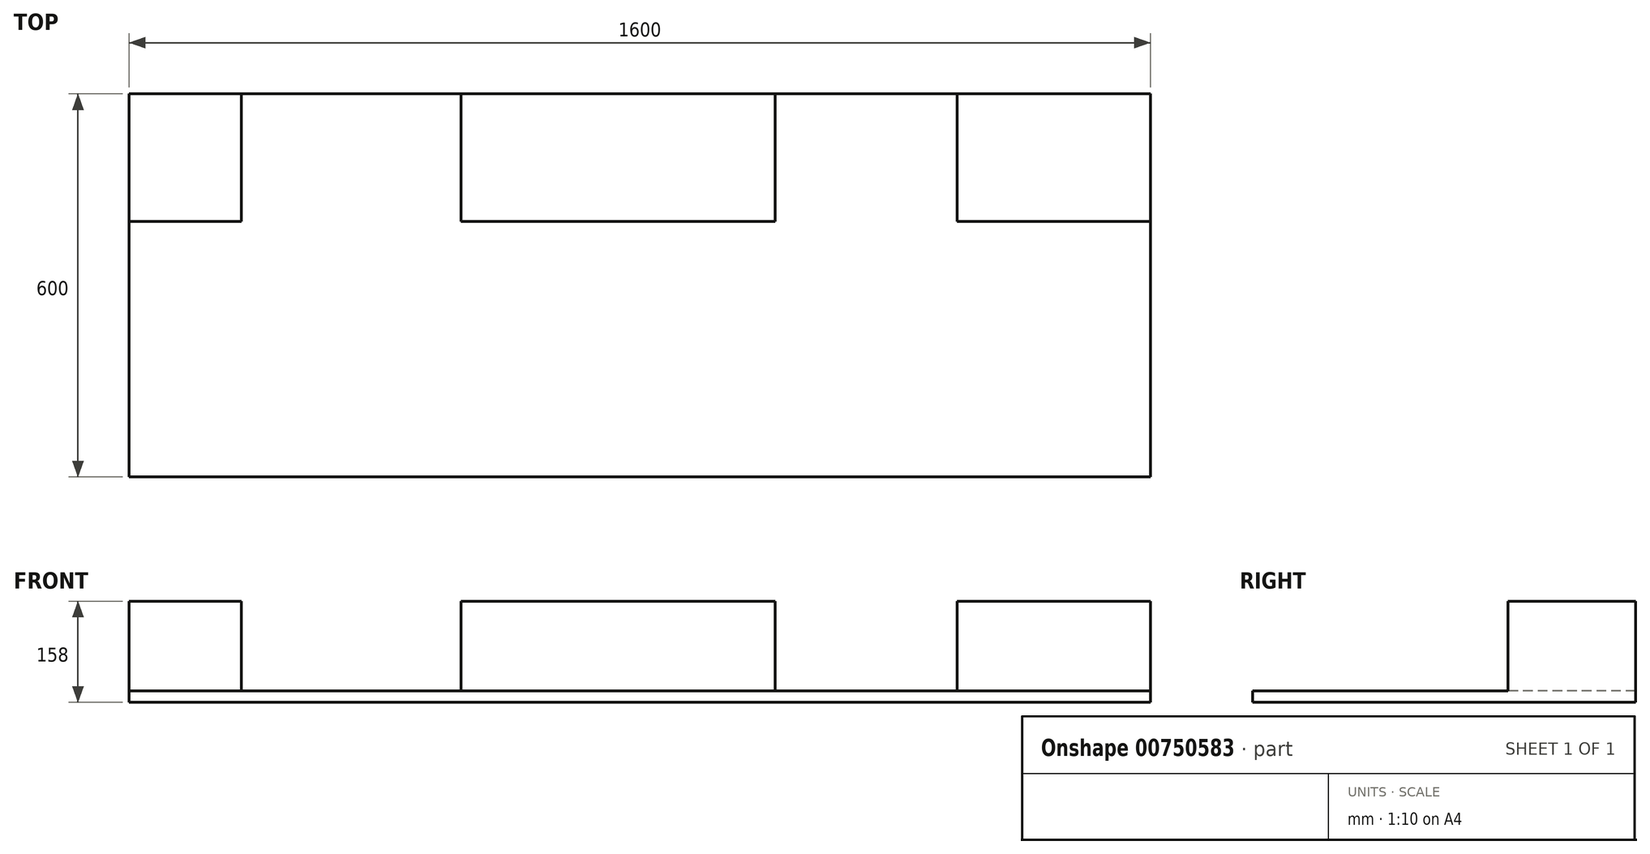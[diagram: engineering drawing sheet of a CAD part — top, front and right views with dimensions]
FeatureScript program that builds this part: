
annotation { "Feature Type Name" : "Feature", "Feature Type Description" : "" }
export const myFeature = defineFeature(function(context is Context, id is Id, definition is map)
    precondition{}
    {
        {
            var Q0;
            Q0=qCreatedBy(makeId("Top.planeOp"),FACE);
            var sketch = newSketch(context, id + "F0", { "sketchPlane" : qUnion([Q0])});
            skLineSegment(sketch, "E0.bottom", {"start": v(800, -300) * mm, "end": v(-800, -300) * mm});
            skLineSegment(sketch, "E0.top", {"start": v(800, 300) * mm, "end": v(-800, 300) * mm});
            skLineSegment(sketch, "E0.left", {"start": v(800, -300) * mm, "end": v(800, 300) * mm});
            skLineSegment(sketch, "E0.right", {"start": v(-800, -300) * mm, "end": v(-800, 300) * mm});
            skPoint(sketch, "E0.middle", {"position": v(0, 0) * mm});
            skSolve(sketch);
        }
        {
            var Q0;
            Q0=qSketchRegion(id+"F0",true);
            extrude(context, id + "F1", {"entities" : qUnion([Q0]), "depth" : 18 * mm, "offsetDistance" : 25 * mm});
        }
        {
            var Q0;
            Q0=makeQuery(id+"F1.opExtrude","CAP_FACE",FACE,{"disambiguationData":[OSD([sQuery(id+"F0.wireOp",EDGE,"E0.bottom"),sQuery(id+"F0.wireOp",EDGE,"E0.top"),sQuery(id+"F0.wireOp",EDGE,"E0.left"),sQuery(id+"F0.wireOp",EDGE,"E0.right")])],"isStart":false});
            var sketch = newSketch(context, id + "F2", { "sketchPlane" : qUnion([Q0])});
            skLineSegment(sketch, "E1.bottom", {"start": v(-800, 300) * mm, "end": v(-624.22, 300) * mm});
            skLineSegment(sketch, "E1.top", {"start": v(-800, 100) * mm, "end": v(-624.22, 100) * mm});
            skLineSegment(sketch, "E1.left", {"start": v(-800, 300) * mm, "end": v(-800, 100) * mm});
            skLineSegment(sketch, "E1.right", {"start": v(-624.22, 300) * mm, "end": v(-624.22, 100) * mm});
            skLineSegment(sketch, "E2.bottom", {"start": v(800, 300) * mm, "end": v(497, 300) * mm});
            skLineSegment(sketch, "E2.top", {"start": v(800, 100) * mm, "end": v(497, 100) * mm});
            skLineSegment(sketch, "E2.left", {"start": v(800, 300) * mm, "end": v(800, 100) * mm});
            skLineSegment(sketch, "E2.right", {"start": v(497, 300) * mm, "end": v(497, 100) * mm});
            skLineSegment(sketch, "E3.bottom", {"start": v(-280.3, 300) * mm, "end": v(212.39, 300) * mm});
            skLineSegment(sketch, "E3.top", {"start": v(-280.3, 100) * mm, "end": v(212.39, 100) * mm});
            skLineSegment(sketch, "E3.left", {"start": v(-280.3, 300) * mm, "end": v(-280.3, 100) * mm});
            skLineSegment(sketch, "E3.right", {"start": v(212.39, 300) * mm, "end": v(212.39, 100) * mm});
            skSolve(sketch);
        }
        {
            var Q0;
            Q0=makeQuery(id+"F2.imprint","IMPRINT",FACE,{"disambiguationData":[TD([[makeQuery(id+"F2.imprint","IMPRINT",EDGE,{"derivedFrom":sQuery(id+"F2.wireOp",EDGE,"E2.bottom")}),1.0]])]});
            var Q1;
            Q1=makeQuery(id+"F2.imprint","IMPRINT",FACE,{"disambiguationData":[TD([[makeQuery(id+"F2.imprint","IMPRINT",EDGE,{"derivedFrom":sQuery(id+"F2.wireOp",EDGE,"E3.bottom")}),1.0]])]});
            var Q2;
            Q2=makeQuery(id+"F2.imprint","IMPRINT",FACE,{"disambiguationData":[TD([[makeQuery(id+"F2.imprint","IMPRINT",EDGE,{"derivedFrom":sQuery(id+"F2.wireOp",EDGE,"E1.bottom")}),1.0]])]});
            extrude(context, id + "F3", {"entities" : qUnion([Q0, Q1, Q2]), "operationType" : NewBodyOperationType.ADD, "depth" : 140 * mm, "offsetDistance" : 25 * mm});
        }
    });
